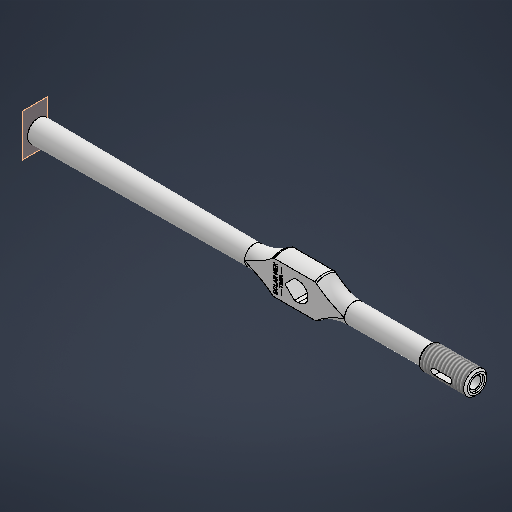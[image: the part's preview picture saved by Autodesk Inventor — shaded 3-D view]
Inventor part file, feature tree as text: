
AUTODESK INVENTOR PART (.ipt)
format: ipt  version: 2025.3 (Build 293356000, 356)  size: 445,440 bytes
history: native  units: mm
features: sketch x3, extrude x2, revolve x1, thread x1, other x1, plane x1, fillet x1, projected_geometry x1
ambient origin geometry x8: Origin, YZ Plane, XZ Plane, XY Plane, X Axis, Y Axis, Z Axis, Center Point
bodies: Solid1 (feature_tree)
feature tree (11):
  sketch  "Sketch1"  dims[d0=7.071068mm d3=2.071068mm]
  revolve  "Revolution1"  [1 undecoded]
  extrude  "Extrusion1"  Depth=52.0mm
  extrude  "Extrusion2"  Depth=1.5mm
  thread  "Thread1"  [1 undecoded]
  other  "Mark2"
  plane  "Work Plane1"
  fillet  "Fillet3"  Radius=6.0mm
  sketch  "Sketch2"  dims[d4=0.066855mm d6=52.0mm]
  sketch  "Sketch4"  dims[d7=10.0mm d8=20.0mm d11=5.0mm d17=6.0mm d20=1.5mm d21=1.0mm d24=1.0mm d25=12.0mm d26=1.0mm d27=1.0mm d28=90.0mm d29=25.0mm d32=360.0deg d33=3.0mm d34=8.0mm d35=0.0mm d36=0.0mm d37=10.0mm d38=0.0mm d39=0.0mm d40=10.0mm d41=11.5mm d42=140.0mm d43=23.0mm d44=0.0mm d46=8.0mm d47=1.0mm d48=50.0mm d49=2.0mm d50=10.0mm d52=10.0mm d54=129.0mm d55=79.0mm d56=1.5mm d57=22.0mm d59=14.930565mm d60=4.048188mm d61=3.0mm]
  projected_geometry  "Projected Loop1"
note: 2 required parameter values undecoded (feature->parameter linkage not recoverable at this tier; creation-order binding heuristic only, values carry confidence <= 0.55)